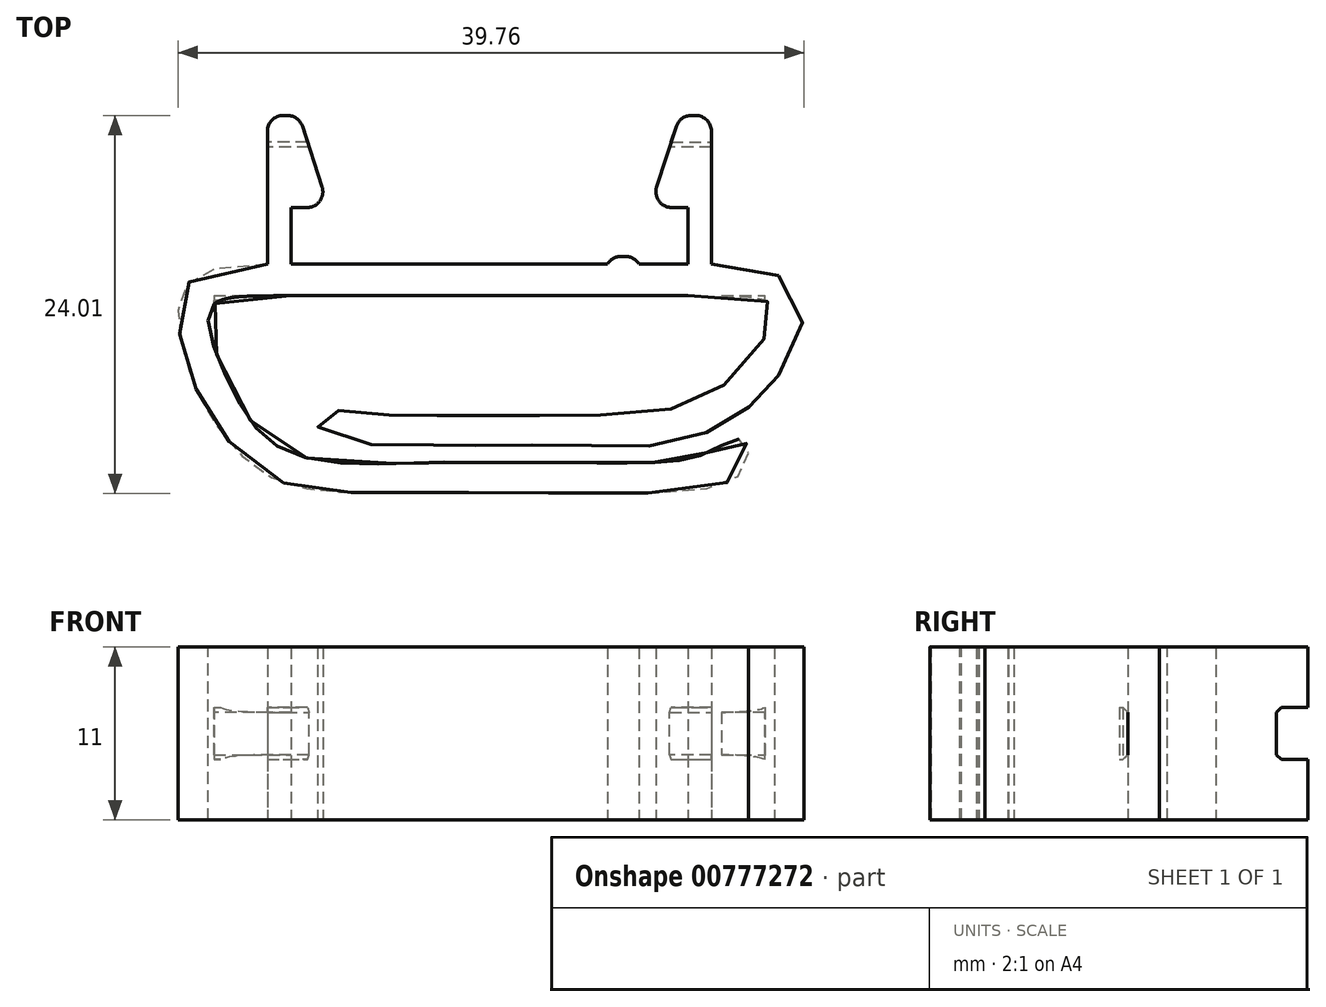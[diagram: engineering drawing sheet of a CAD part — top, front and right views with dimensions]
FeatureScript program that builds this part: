
annotation { "Feature Type Name" : "Feature", "Feature Type Description" : "" }
export const myFeature = defineFeature(function(context is Context, id is Id, definition is map)
    precondition{}
    {
        {
            var Q0;
            Q0=qCreatedBy(makeId("Top.planeOp"),FACE);
            var sketch = newSketch(context, id + "F0", { "sketchPlane" : qUnion([Q0])});
            skLineSegment(sketch, "E0", {"start": v(-14.1, 0) * mm, "end": v(-14.1, 9.45) * mm});
            skLineSegment(sketch, "E1", {"start": v(-14.1, 9.45) * mm, "end": v(-12.1, 9.45) * mm});
            skLineSegment(sketch, "E2", {"start": v(-12.1, 9.45) * mm, "end": v(-10.2, 3.6) * mm});
            skLineSegment(sketch, "E3", {"start": v(-10.2, 3.6) * mm, "end": v(-12.6, 3.6) * mm});
            skLineSegment(sketch, "E4", {"start": v(-12.6, 3.6) * mm, "end": v(-12.6, 0) * mm});
            skLineSegment(sketch, "E5", {"start": v(-12.6, 0) * mm, "end": v(0, 0) * mm});
            skLineSegment(sketch, "E6.MirrorCS", {"start": v(12.6, 0) * mm, "end": v(0, 0) * mm});
            skLineSegment(sketch, "E7.MirrorCS", {"start": v(12.6, 3.6) * mm, "end": v(12.6, 0) * mm});
            skLineSegment(sketch, "E8.MirrorCS", {"start": v(10.2, 3.6) * mm, "end": v(12.6, 3.6) * mm});
            skLineSegment(sketch, "E9.MirrorCS", {"start": v(12.1, 9.45) * mm, "end": v(10.2, 3.6) * mm});
            skLineSegment(sketch, "E10.MirrorCS", {"start": v(14.1, 9.45) * mm, "end": v(12.1, 9.45) * mm});
            skLineSegment(sketch, "E11.MirrorCS", {"start": v(14.1, 0) * mm, "end": v(14.1, 9.45) * mm});
            skLineSegment(sketch, "E12", {"start": v(-12.6, -2) * mm, "end": v(12.6, -2) * mm});
            skLineSegment(sketch, "E13.bottom", {"start": v(-9.5, 0) * mm, "end": v(-7.5, 0) * mm});
            skLineSegment(sketch, "E13.top", {"start": v(-9.5, 0.5) * mm, "end": v(-7.5, 0.5) * mm});
            skLineSegment(sketch, "E13.left", {"start": v(-9.5, 0) * mm, "end": v(-9.5, 0.5) * mm});
            skLineSegment(sketch, "E13.right", {"start": v(-7.5, 0) * mm, "end": v(-7.5, 0.5) * mm});
            skLineSegment(sketch, "E14.MirrorCS", {"start": v(9.5, 0) * mm, "end": v(9.5, 0.5) * mm});
            skLineSegment(sketch, "E15.MirrorCS", {"start": v(9.5, 0.5) * mm, "end": v(7.5, 0.5) * mm});
            skLineSegment(sketch, "E16.MirrorCS", {"start": v(7.5, 0) * mm, "end": v(7.5, 0.5) * mm});
            skFitSpline(sketch, "E17", {"points": [v(-14.1, 0) * mm, v(-19.6, -2) * mm, v(-19.3, -6) * mm, v(-17.8, -9.5) * mm, v(-14, -13.47) * mm, v(-8.6, -14.5) * mm, v(-4.16, -14.5) * mm, v(0, -14.5) * mm, v(10.62, -14.5) * mm, v(16.16, -13.05) * mm, v(16.12, -11.15) * mm, v(13.83, -11.97) * mm, v(10.18, -12.6) * mm, v(4.24, -12.6) * mm, v(0, -12.6) * mm, v(-4.14, -12.6) * mm, v(-12.63, -12) * mm, v(-16.3, -8) * mm, v(-17.8, -3) * mm, v(-12.6, -2) * mm], "startDerivative": vector(-187.4, 0) * mm, "endDerivative": vector(178.4, 1.35) * mm});
            skPoint(sketch, "E18.5.internal.snap0", {"position": v(-11.15, 6.52) * mm});
            skPoint(sketch, "E18.6.internal.snap0", {"position": v(-11.15, 6.52) * mm});
            skFitSpline(sketch, "E18", {"points": [v(12.6, -2) * mm, v(18.1, -3) * mm, v(16.1, -6.5) * mm, v(12.4, -9) * mm, v(5.87, -9.6) * mm, v(1.52, -9.6) * mm, v(-2.3, -9.6) * mm, v(-5.05, -9.6) * mm, v(-8.84, -9.39) * mm, v(-10.61, -9.42) * mm, v(-10.68, -10.68) * mm, v(-4.78, -11.5) * mm, v(-2.32, -11.5) * mm, v(1.28, -11.5) * mm, v(6.14, -11.5) * mm, v(10.69, -11.5) * mm, v(15, -10.1) * mm, v(17.2, -8.4) * mm, v(19, -6) * mm, v(19.6, -1.6) * mm, v(14.1, 0) * mm], "startDerivative": vector(190.28, 1.47) * mm, "endDerivative": vector(-73.18, 0) * mm});
            skLineSegment(sketch, "E19", {"start": v(-32.46, -14) * mm, "end": v(40.18, -14) * mm, "construction": true});
            skLineSegment(sketch, "E20", {"start": v(-32.46, -11.5) * mm, "end": v(40.03, -11.5) * mm, "construction": true});
            skSolve(sketch);
        }
        {
            var Q0;
            Q0=makeQuery(id+"F0.imprint","IMPRINT",FACE,{"disambiguationData":[TD([[makeQuery(id+"F0.imprint","IMPRINT",EDGE,{"derivedFrom":sQuery(id+"F0.wireOp",EDGE,"E0")}),-1.0]])]});
            var Q1;
            Q1=makeQuery(id+"F0.imprint","IMPRINT",FACE,{"disambiguationData":[TD([[makeQuery(id+"F0.imprint","IMPRINT",EDGE,{"derivedFrom":sQuery(id+"F0.wireOp",EDGE,"E13.bottom")}),1.0]])]});
            var Q2;
            {var subQ0=sQuery(id+"F0.wireOp",EDGE,"E14.MirrorCS");Q2=makeQuery(id+"F0.imprint","IMPRINT",FACE,{"disambiguationData":[TD([[makeQuery(id+"F0.imprint","IMPRINT",EDGE,{"derivedFrom":subQ0}),1.0]])]});}
            extrude(context, id + "F1", {"entities" : qUnion([Q0, Q1, Q2]), "depth" : 11 * mm, "offsetDistance" : 25 * mm});
        }
        {
            var Q0;
            Q0=makeQuery(id+"F1.opExtrude","SWEPT_EDGE",EDGE,{"disambiguationData":[OSD([sQuery(id+"F0.wireOp",EDGE,"E2"),sQuery(id+"F0.wireOp",EDGE,"E3")])]});
            var Q1;
            Q1=makeQuery(id+"F1.opExtrude","SWEPT_EDGE",EDGE,{"disambiguationData":[OSD([sQuery(id+"F0.wireOp",EDGE,"E0"),sQuery(id+"F0.wireOp",EDGE,"E1")])]});
            var Q2;
            Q2=makeQuery(id+"F1.opExtrude","SWEPT_EDGE",EDGE,{"disambiguationData":[OSD([sQuery(id+"F0.wireOp",EDGE,"E1"),sQuery(id+"F0.wireOp",EDGE,"E2")])]});
            var Q3;
            Q3=makeQuery(id+"F1.opExtrude","SWEPT_EDGE",EDGE,{"disambiguationData":[OSD([sQuery(id+"F0.wireOp",EDGE,"E13.top"),sQuery(id+"F0.wireOp",EDGE,"E13.left")])]});
            var Q4;
            Q4=makeQuery(id+"F1.opExtrude","SWEPT_EDGE",EDGE,{"disambiguationData":[OSD([sQuery(id+"F0.wireOp",EDGE,"E13.top"),sQuery(id+"F0.wireOp",EDGE,"E13.right")])]});
            var Q5;
            Q5=makeQuery(id+"F1.opExtrude","SWEPT_EDGE",EDGE,{"disambiguationData":[OSD([sQuery(id+"F0.wireOp",EDGE,"E15.MirrorCS"),sQuery(id+"F0.wireOp",EDGE,"E16.MirrorCS")])]});
            var Q6;
            Q6=makeQuery(id+"F1.opExtrude","SWEPT_EDGE",EDGE,{"disambiguationData":[OSD([sQuery(id+"F0.wireOp",EDGE,"E14.MirrorCS"),sQuery(id+"F0.wireOp",EDGE,"E15.MirrorCS")])]});
            var Q7;
            Q7=makeQuery(id+"F1.opExtrude","SWEPT_EDGE",EDGE,{"disambiguationData":[OSD([sQuery(id+"F0.wireOp",EDGE,"E8.MirrorCS"),sQuery(id+"F0.wireOp",EDGE,"E9.MirrorCS")])]});
            var Q8;
            Q8=makeQuery(id+"F1.opExtrude","SWEPT_EDGE",EDGE,{"disambiguationData":[OSD([sQuery(id+"F0.wireOp",EDGE,"E9.MirrorCS"),sQuery(id+"F0.wireOp",EDGE,"E10.MirrorCS")])]});
            var Q9;
            Q9=makeQuery(id+"F1.opExtrude","SWEPT_EDGE",EDGE,{"disambiguationData":[OSD([sQuery(id+"F0.wireOp",EDGE,"E10.MirrorCS"),sQuery(id+"F0.wireOp",EDGE,"E11.MirrorCS")])]});
            fillet(context, id + "F2", {"entities" : qUnion([Q0, Q1, Q2, Q3, Q4, Q5, Q6, Q7, Q8, Q9]), "radius" : 1 * mm, "tangentPropagation" : true, "allowEdgeOverflow" : false});
        }
        {
            var Q0;
            Q0=qCreatedBy(makeId("Right.planeOp"),FACE);
            var sketch = newSketch(context, id + "F3", { "sketchPlane" : qUnion([Q0])});
            skLineSegment(sketch, "E21.bottom", {"start": v(-4, 3.85) * mm, "end": v(-2, 3.85) * mm});
            skLineSegment(sketch, "E21.top", {"start": v(-4, 7.15) * mm, "end": v(-2, 7.15) * mm});
            skLineSegment(sketch, "E21.left", {"start": v(-4, 3.85) * mm, "end": v(-4, 7.15) * mm});
            skLineSegment(sketch, "E21.right", {"start": v(-2, 3.85) * mm, "end": v(-2, 7.15) * mm});
            skPoint(sketch, "E21.middle", {"position": v(-3, 5.5) * mm});
            skLineSegment(sketch, "E22.bottom", {"start": v(7.45, 3.85) * mm, "end": v(9.45, 3.85) * mm});
            skLineSegment(sketch, "E22.top", {"start": v(7.45, 7.15) * mm, "end": v(9.45, 7.15) * mm});
            skLineSegment(sketch, "E22.left", {"start": v(7.45, 3.85) * mm, "end": v(7.45, 7.15) * mm});
            skLineSegment(sketch, "E22.right", {"start": v(9.45, 3.85) * mm, "end": v(9.45, 7.15) * mm});
            skPoint(sketch, "E22.middle", {"position": v(8.45, 5.5) * mm});
            skSolve(sketch);
        }
        {
            var Q0;
            Q0=qSketchRegion(id+"F3",true);
            extrude(context, id + "F4", {"entities" : qUnion([Q0]), "operationType" : NewBodyOperationType.REMOVE, "endBound" : BoundingType.SYMMETRIC, "oppositeDirection" : true, "depth" : 35 * mm, "offsetDistance" : 25 * mm});
        }
        {
            var Q0;
            {var subQ0=sQuery(id+"F3.wireOp",EDGE,"E21.bottom");var subQ1=sQuery(id+"F3.wireOp",EDGE,"E21.left");Q0=makeQuery(id+"F4.boolean.opBoolean","COPY",EDGE,{"disambiguationData":[TD([makeQuery(id+"F1.opExtrude","SWEPT_FACE",FACE,{"disambiguationData":[OSD([sQuery(id+"F0.wireOp",EDGE,"E17")])]})])],"derivedFrom":makeQuery(id+"F4.opExtrude","SWEPT_EDGE",EDGE,{"disambiguationData":[OSD([subQ0,subQ1])]})});}
            var Q1;
            {var subQ0=sQuery(id+"F3.wireOp",EDGE,"E21.top");var subQ1=sQuery(id+"F3.wireOp",EDGE,"E21.right");Q1=makeQuery(id+"F4.boolean.opBoolean","COPY",EDGE,{"disambiguationData":[TD([makeQuery(id+"F1.opExtrude","SWEPT_FACE",FACE,{"disambiguationData":[OSD([sQuery(id+"F0.wireOp",EDGE,"E17")])]})])],"derivedFrom":makeQuery(id+"F4.opExtrude","SWEPT_EDGE",EDGE,{"disambiguationData":[OSD([subQ0,subQ1])]})});}
            var Q2;
            {var subQ0=sQuery(id+"F3.wireOp",EDGE,"E21.top");var subQ1=sQuery(id+"F3.wireOp",EDGE,"E21.left");Q2=makeQuery(id+"F4.boolean.opBoolean","COPY",EDGE,{"disambiguationData":[TD([makeQuery(id+"F1.opExtrude","SWEPT_FACE",FACE,{"disambiguationData":[OSD([sQuery(id+"F0.wireOp",EDGE,"E17")])]})])],"derivedFrom":makeQuery(id+"F4.opExtrude","SWEPT_EDGE",EDGE,{"disambiguationData":[OSD([subQ0,subQ1])]})});}
            var Q3;
            {var subQ0=sQuery(id+"F3.wireOp",EDGE,"E21.bottom");var subQ1=sQuery(id+"F3.wireOp",EDGE,"E21.right");Q3=makeQuery(id+"F4.boolean.opBoolean","COPY",EDGE,{"disambiguationData":[TD([makeQuery(id+"F1.opExtrude","SWEPT_FACE",FACE,{"disambiguationData":[OSD([sQuery(id+"F0.wireOp",EDGE,"E17")])]})])],"derivedFrom":makeQuery(id+"F4.opExtrude","SWEPT_EDGE",EDGE,{"disambiguationData":[OSD([subQ0,subQ1])]})});}
            var Q4;
            {var subQ0=sQuery(id+"F3.wireOp",EDGE,"E22.bottom");var subQ1=sQuery(id+"F3.wireOp",EDGE,"E22.left");Q4=makeQuery(id+"F4.boolean.opBoolean","COPY",EDGE,{"disambiguationData":[TD([makeQuery(id+"F1.opExtrude","SWEPT_FACE",FACE,{"disambiguationData":[OSD([sQuery(id+"F0.wireOp",EDGE,"E0")])]})])],"derivedFrom":makeQuery(id+"F4.opExtrude","SWEPT_EDGE",EDGE,{"disambiguationData":[OSD([subQ0,subQ1])]})});}
            var Q5;
            {var subQ0=sQuery(id+"F3.wireOp",EDGE,"E22.top");var subQ1=sQuery(id+"F3.wireOp",EDGE,"E22.left");Q5=makeQuery(id+"F4.boolean.opBoolean","COPY",EDGE,{"disambiguationData":[TD([makeQuery(id+"F1.opExtrude","SWEPT_FACE",FACE,{"disambiguationData":[OSD([sQuery(id+"F0.wireOp",EDGE,"E0")])]})])],"derivedFrom":makeQuery(id+"F4.opExtrude","SWEPT_EDGE",EDGE,{"disambiguationData":[OSD([subQ0,subQ1])]})});}
            var Q6;
            {var subQ0=sQuery(id+"F3.wireOp",EDGE,"E22.left");var subQ1=sQuery(id+"F3.wireOp",EDGE,"E22.top");Q6=makeQuery(id+"F4.boolean.opBoolean","COPY",EDGE,{"disambiguationData":[TD([makeQuery(id+"F1.opExtrude","SWEPT_FACE",FACE,{"disambiguationData":[OSD([sQuery(id+"F0.wireOp",EDGE,"E9.MirrorCS")])]})])],"derivedFrom":makeQuery(id+"F4.opExtrude","SWEPT_EDGE",EDGE,{"disambiguationData":[OSD([subQ1,subQ0])]})});}
            var Q7;
            {var subQ0=sQuery(id+"F3.wireOp",EDGE,"E22.left");var subQ1=sQuery(id+"F3.wireOp",EDGE,"E22.bottom");Q7=makeQuery(id+"F4.boolean.opBoolean","COPY",EDGE,{"disambiguationData":[TD([makeQuery(id+"F1.opExtrude","SWEPT_FACE",FACE,{"disambiguationData":[OSD([sQuery(id+"F0.wireOp",EDGE,"E9.MirrorCS")])]})])],"derivedFrom":makeQuery(id+"F4.opExtrude","SWEPT_EDGE",EDGE,{"disambiguationData":[OSD([subQ1,subQ0])]})});}
            var Q8;
            {var subQ0=sQuery(id+"F3.wireOp",EDGE,"E21.top");var subQ1=sQuery(id+"F3.wireOp",EDGE,"E21.right");Q8=makeQuery(id+"F4.boolean.opBoolean","COPY",EDGE,{"disambiguationData":[TD([makeQuery(id+"F1.opExtrude","SWEPT_FACE",FACE,{"disambiguationData":[OSD([sQuery(id+"F0.wireOp",EDGE,"E18")])]})])],"derivedFrom":makeQuery(id+"F4.opExtrude","SWEPT_EDGE",EDGE,{"disambiguationData":[OSD([subQ0,subQ1])]})});}
            var Q9;
            {var subQ0=sQuery(id+"F3.wireOp",EDGE,"E21.top");var subQ1=sQuery(id+"F3.wireOp",EDGE,"E21.left");Q9=makeQuery(id+"F4.boolean.opBoolean","COPY",EDGE,{"disambiguationData":[TD([makeQuery(id+"F1.opExtrude","SWEPT_FACE",FACE,{"disambiguationData":[OSD([sQuery(id+"F0.wireOp",EDGE,"E18")])]})])],"derivedFrom":makeQuery(id+"F4.opExtrude","SWEPT_EDGE",EDGE,{"disambiguationData":[OSD([subQ0,subQ1])]})});}
            var Q10;
            {var subQ0=sQuery(id+"F3.wireOp",EDGE,"E21.bottom");var subQ1=sQuery(id+"F3.wireOp",EDGE,"E21.left");Q10=makeQuery(id+"F4.boolean.opBoolean","COPY",EDGE,{"disambiguationData":[TD([makeQuery(id+"F1.opExtrude","SWEPT_FACE",FACE,{"disambiguationData":[OSD([sQuery(id+"F0.wireOp",EDGE,"E18")])]})])],"derivedFrom":makeQuery(id+"F4.opExtrude","SWEPT_EDGE",EDGE,{"disambiguationData":[OSD([subQ0,subQ1])]})});}
            var Q11;
            {var subQ0=sQuery(id+"F3.wireOp",EDGE,"E21.bottom");var subQ1=sQuery(id+"F3.wireOp",EDGE,"E21.right");Q11=makeQuery(id+"F4.boolean.opBoolean","COPY",EDGE,{"disambiguationData":[TD([makeQuery(id+"F1.opExtrude","SWEPT_FACE",FACE,{"disambiguationData":[OSD([sQuery(id+"F0.wireOp",EDGE,"E18")])]})])],"derivedFrom":makeQuery(id+"F4.opExtrude","SWEPT_EDGE",EDGE,{"disambiguationData":[OSD([subQ0,subQ1])]})});}
            chamfer(context, id + "F5", {"entities" : qUnion([Q0, Q1, Q2, Q3, Q4, Q5, Q6, Q7, Q8, Q9, Q10, Q11]), "width" : .3 * mm, "tangentPropagation" : true});
        }
    });
